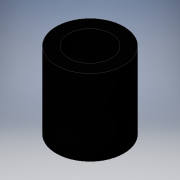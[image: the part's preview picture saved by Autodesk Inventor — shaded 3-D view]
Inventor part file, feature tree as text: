
AUTODESK INVENTOR PART (.ipt)
format: ipt  version: 2016 (Build 200138000, 138)  size: 91,136 bytes
history: native  units: mm
features: extrude x1, sketch x1
ambient origin geometry x8: Origin, YZ Plane, XZ Plane, XY Plane, X Axis, Y Axis, Z Axis, Center Point
bodies: Volumenkörper1 (feature_tree)
feature tree (2):
  extrude  "Extrusion1"  Depth=6.1mm
  sketch  "Skizze1"  dims[d0=1.0mm d1=3.4mm d2=6.1mm d3=0.0mm]
